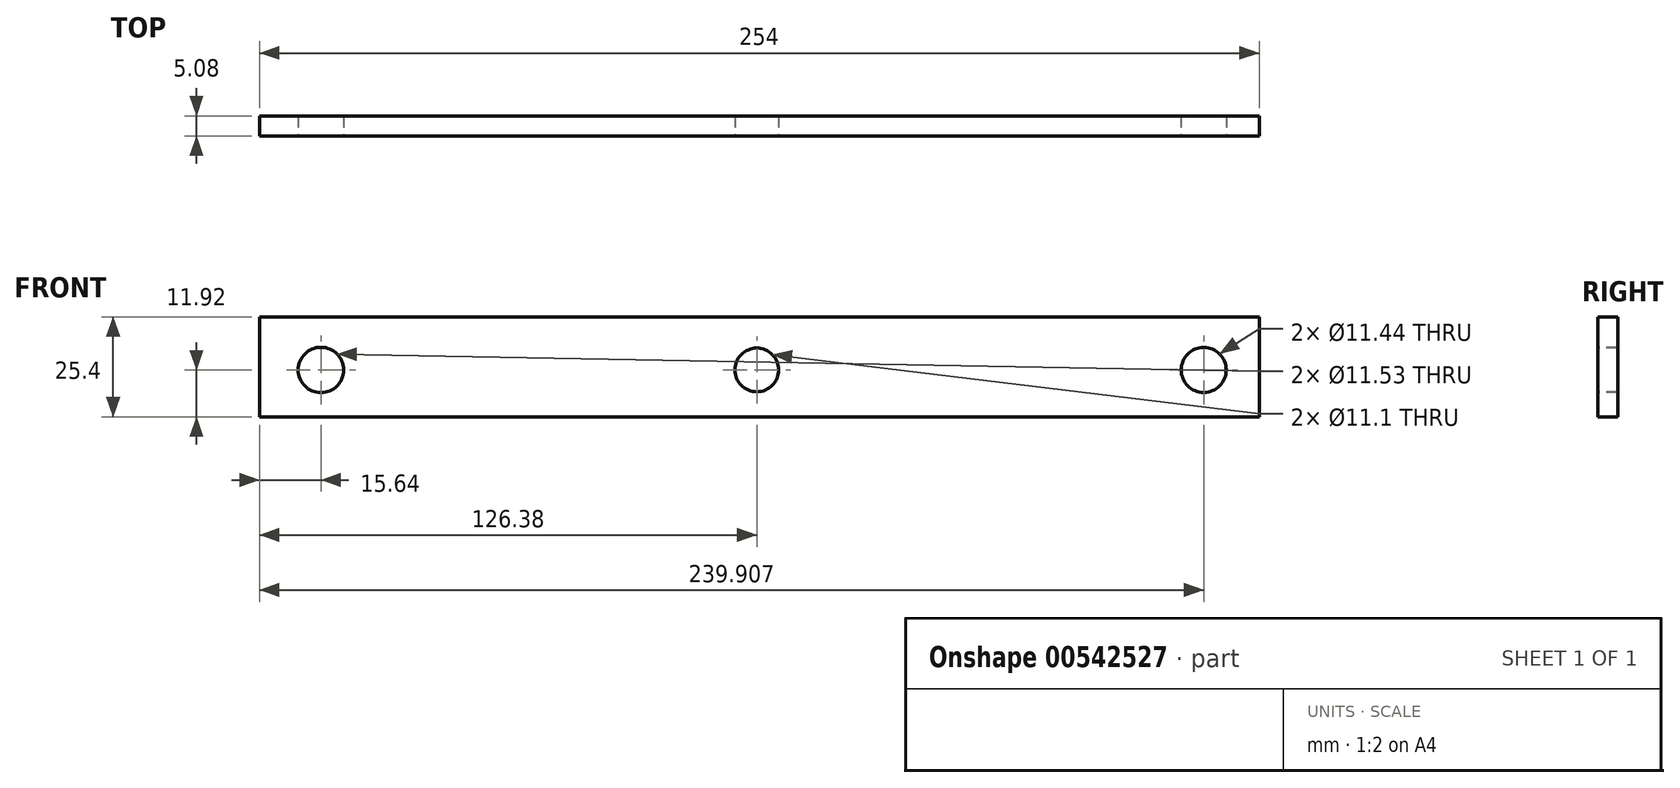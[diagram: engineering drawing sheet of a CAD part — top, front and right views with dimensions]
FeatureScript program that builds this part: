
annotation { "Feature Type Name" : "Feature", "Feature Type Description" : "" }
export const myFeature = defineFeature(function(context is Context, id is Id, definition is map)
    precondition{}
    {
        {
            var Q0;
            Q0=qCreatedBy(makeId("Front.planeOp"),FACE);
            var sketch = newSketch(context, id + "F0", { "sketchPlane" : qUnion([Q0])});
            skLineSegment(sketch, "E0.bottom", {"start": v(-126.38, 13.48) * mm, "end": v(127.62, 13.48) * mm});
            skLineSegment(sketch, "E0.top", {"start": v(-126.38, -11.92) * mm, "end": v(127.62, -11.92) * mm});
            skLineSegment(sketch, "E0.left", {"start": v(-126.38, 13.48) * mm, "end": v(-126.38, -11.92) * mm});
            skLineSegment(sketch, "E0.right", {"start": v(127.62, 13.48) * mm, "end": v(127.62, -11.92) * mm});
            skPoint(sketch, "E0.middle", {"position": v(0.62, 0.78) * mm});
            skSolve(sketch);
        }
        {
            var Q0;
            Q0 = qSketchRegion(id + "F0", true);
            extrude(context, id + "F1", {"entities" : qUnion([Q0]), "endBound" : BoundingType.SYMMETRIC, "oppositeDirection" : true, "depth" : 5.08 * mm, "offsetDistance" : 25.4 * mm});
        }
        {
            var Q0;
            Q0=makeQuery(id+"F1.opExtrude","CAP_FACE",FACE,{"disambiguationData":[OSD([sQuery(id+"F0.wireOp",EDGE,"E0.bottom"),sQuery(id+"F0.wireOp",EDGE,"E0.top"),sQuery(id+"F0.wireOp",EDGE,"E0.left"),sQuery(id+"F0.wireOp",EDGE,"E0.right")])],"isStart":true});
            var sketch = newSketch(context, id + "F2", { "sketchPlane" : qUnion([Q0])});
            skCircle(sketch, "E1", {"center": v(-110.74, 0) * mm, "radius": 5.77 * mm});
            skCircle(sketch, "E2", {"center": v(113.53, 0) * mm, "radius": 5.72 * mm});
            skSolve(sketch);
        }
        {
            var Q0;
            Q0 = qSketchRegion(id + "F2", true);
            extrude(context, id + "F3", {"entities" : qUnion([Q0]), "operationType" : NewBodyOperationType.REMOVE, "oppositeDirection" : true, "depth" : 38.1 * mm, "offsetDistance" : 25.4 * mm});
        }
        {
            var Q0;
            Q0=makeQuery(id+"F1.opExtrude","CAP_FACE",FACE,{"disambiguationData":[OSD([sQuery(id+"F0.wireOp",EDGE,"E0.bottom"),sQuery(id+"F0.wireOp",EDGE,"E0.top"),sQuery(id+"F0.wireOp",EDGE,"E0.left"),sQuery(id+"F0.wireOp",EDGE,"E0.right")])],"isStart":true});
            var sketch = newSketch(context, id + "F4", { "sketchPlane" : qUnion([Q0])});
            skCircle(sketch, "E3", {"center": v(0, 0) * mm, "radius": 5.55 * mm});
            skSolve(sketch);
        }
        {
            var Q0;
            Q0 = qSketchRegion(id + "F4", true);
            extrude(context, id + "F5", {"entities" : qUnion([Q0]), "operationType" : NewBodyOperationType.REMOVE, "oppositeDirection" : true, "depth" : 25.4 * mm, "offsetDistance" : 25.4 * mm});
        }
    });
